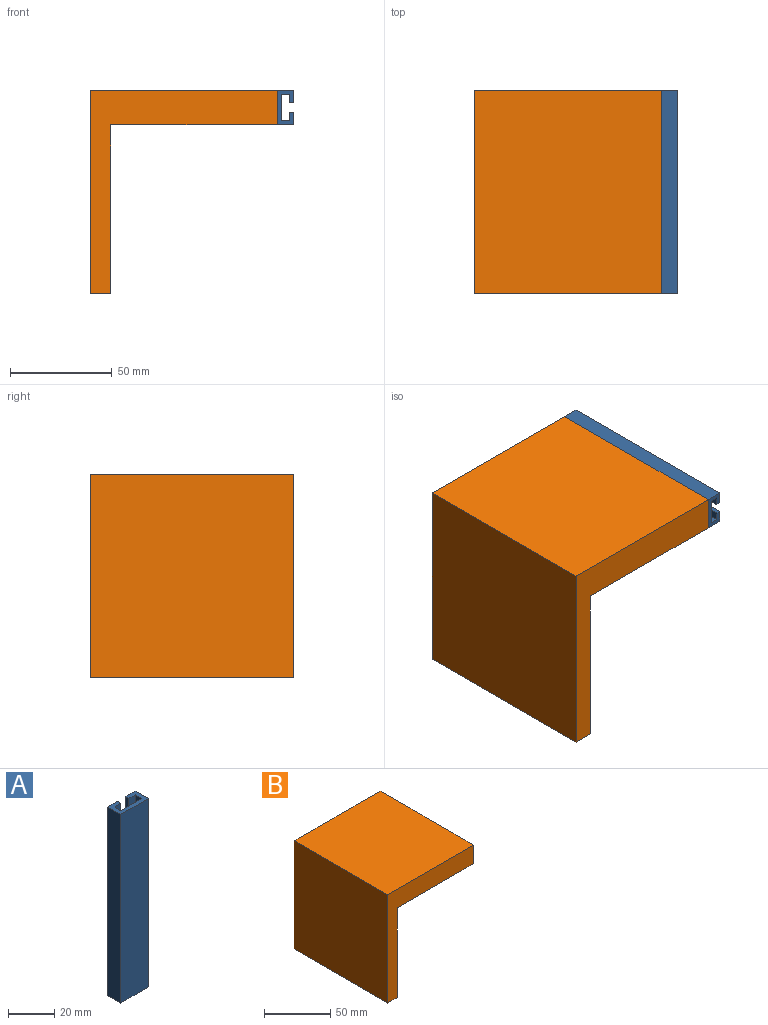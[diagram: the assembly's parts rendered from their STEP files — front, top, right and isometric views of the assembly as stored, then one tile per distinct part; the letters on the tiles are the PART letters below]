
ASSEMBLY  parts=2 mates=1
PART A: 14 faces, bbox 17x8x100 mm
  f0: plane 100x6mm, normal (0,1,0), area 600mm2, adj f1,f11,f12,f13
  f1: plane 100x8mm, normal (-1,0,0), area 800mm2, adj f0,f2,f12,f13
  f2: plane 100x17mm, normal (0,-1,0), area 1700mm2, adj f1,f3,f12,f13
  f3: plane 100x8mm, normal (1,0,0), area 800mm2, adj f2,f4,f12,f13
  f4: plane 100x6mm, normal (0,1,0), area 600mm2, adj f3,f5,f12,f13
  f5: plane 100x2mm, normal (-1,0,0), area 200mm2, adj f4,f6,f12,f13
  f6: plane 100x4mm, normal (0,-1,0), area 400mm2, adj f5,f7,f12,f13
  f7: plane 100x4mm, normal (-1,0,0), area 400mm2, adj f6,f8,f12,f13
  f8: plane 100x13mm, normal (0,1,0), area 1300mm2, adj f7,f9,f12,f13
  f9: plane 100x4mm, normal (1,0,0), area 400mm2, adj f8,f10,f12,f13
  f10: plane 100x4mm, normal (0,-1,0), area 400mm2, adj f9,f11,f12,f13
  f11: plane 100x2mm, normal (1,0,0), area 200mm2, adj f0,f10,f12,f13
  f12: plane 17x8mm, normal (0,0,1), area 74mm2, adj f0,f1,f2,f3,f4,f5,f6,f7
  f13: plane 17x8mm, normal (0,0,-1), area 74mm2, adj f0,f1,f2,f3,f4,f5,f6,f7
PART B: 8 faces, bbox 92x100x100 mm
  f0: plane 100x83mm, normal (1,0,0), area 8300mm2, adj f1,f5,f6,f7
  f1: plane 100x82mm, normal (0,0,-1), area 8200mm2, adj f0,f2,f6,f7
  f2: plane 100x17mm, normal (1,0,0), area 1700mm2, adj f1,f3,f6,f7
  f3: plane 100x92mm, normal (0,0,1), area 9200mm2, adj f2,f4,f6,f7
  f4: plane 100x100mm, normal (-1,0,0), area 10000mm2, adj f3,f5,f6,f7
  f5: plane 100x10mm, normal (0,0,-1), area 1000mm2, adj f0,f4,f6,f7
  f6: plane 100x92mm, normal (0,-1,0), area 2394mm2, adj f0,f1,f2,f3,f4,f5
  f7: plane 100x92mm, normal (0,1,0), area 2394mm2, adj f0,f1,f2,f3,f4,f5
PLACE A rot(axis=(0.58,0.58,-0.58),120deg) t=(36.99,-0.78,47.57)mm
PLACE B t=(-5.01,-0.78,6.07)mm
MATE fastened A.f2 <-> B.f2  axis (-1,0,0) through (36.99,-0.78,47.57)mm
